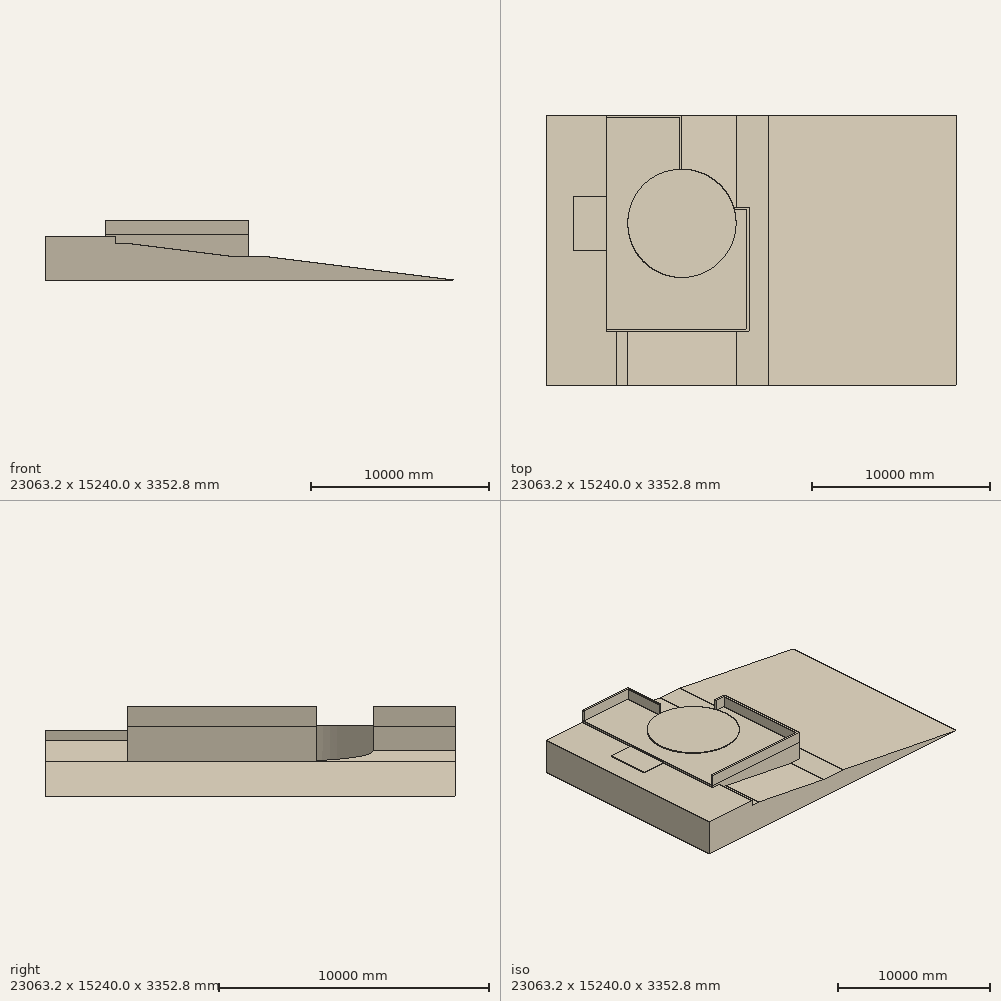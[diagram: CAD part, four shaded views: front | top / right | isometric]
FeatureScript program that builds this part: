
annotation { "Feature Type Name" : "Feature", "Feature Type Description" : "" }
export const myFeature = defineFeature(function(context is Context, id is Id, definition is map)
    precondition{}
    {
        {
            var Q0;
            Q0=qCreatedBy(makeId("Top.planeOp"),FACE);
            var sketch = newSketch(context, id + "F0", { "sketchPlane" : qUnion([Q0])});
            skCircle(sketch, "E0", {"center": v(0, 0) * mm, "radius": 3048 * mm});
            skSolve(sketch);
        }
        {
            var Q0;
            Q0=makeQuery(id+"F0.imprint","IMPRINT",FACE,{"disambiguationData":[TD([[makeQuery(id+"F0.imprint","IMPRINT",EDGE,{"derivedFrom":sQuery(id+"F0.wireOp",EDGE,"E0")}),1.0]])]});
            extrude(context, id + "F1", {"entities" : qUnion([Q0]), "depth" : 1320.8 * mm, "offsetDistance" : 25.4 * mm});
        }
        {
            var Q0;
            Q0=qCreatedBy(makeId("Front.planeOp"),FACE);
            var sketch = newSketch(context, id + "F2", { "sketchPlane" : qUnion([Q0])});
            skLineSegment(sketch, "E1", {"start": v(-3048, 0) * mm, "end": v(-3048, 1320.8) * mm});
            skLineSegment(sketch, "E2", {"start": v(3048, 1320.8) * mm, "end": v(3048, 0) * mm});
            skLineSegment(sketch, "E3", {"start": v(-3048, 762) * mm, "end": v(-3657.6, 762) * mm});
            skLineSegment(sketch, "E4", {"start": v(-3048, 762) * mm, "end": v(3048, 0) * mm});
            skLineSegment(sketch, "E5", {"start": v(-3657.6, 1117.6) * mm, "end": v(-5459.43, 1117.6) * mm});
            skLineSegment(sketch, "E6", {"start": v(-3657.6, 1117.6) * mm, "end": v(-3657.6, 762) * mm});
            skLineSegment(sketch, "E7", {"start": v(-5459.43, 1117.6) * mm, "end": v(-7620, 1117.6) * mm});
            skLineSegment(sketch, "E8", {"start": v(-7620, 1117.6) * mm, "end": v(-7620, -1320.8) * mm});
            skLineSegment(sketch, "E9", {"start": v(-7620, -1320.8) * mm, "end": v(15443.2, -1320.8) * mm});
            skLineSegment(sketch, "E10", {"start": v(3048, 0) * mm, "end": v(4876.8, 0) * mm});
            skLineSegment(sketch, "E11", {"start": v(4876.8, 0) * mm, "end": v(15443.2, -1320.8) * mm});
            skPoint(sketch, "E12.orphan", {"position": v(-7620, 762) * mm});
            skLineSegment(sketch, "E13.0", {"start": v(-3048, 0) * mm, "end": v(3048, 0) * mm, "construction": true});
            skSolve(sketch);
        }
        {
            var Q0;
            Q0 = qSketchRegion(id + "F2", true);
            extrude(context, id + "F3", {"entities" : qUnion([Q0]), "depth" : 9144 * mm, "offsetDistance" : 25.4 * mm});
        }
        {
            var Q0;
            Q0=makeQuery(id+"F3.opExtrude","CAP_FACE",FACE,{"disambiguationData":[OSD([sQuery(id+"F2.wireOp",EDGE,"E3"),sQuery(id+"F2.wireOp",EDGE,"E4"),sQuery(id+"F2.wireOp",EDGE,"E5"),sQuery(id+"F2.wireOp",EDGE,"E6"),sQuery(id+"F2.wireOp",EDGE,"E7"),sQuery(id+"F2.wireOp",EDGE,"E8"),sQuery(id+"F2.wireOp",EDGE,"E9"),sQuery(id+"F2.wireOp",EDGE,"E10"),sQuery(id+"F2.wireOp",EDGE,"E11")])],"isStart":true});
            extrude(context, id + "F4", {"entities" : qUnion([Q0]), "operationType" : NewBodyOperationType.ADD, "depth" : 6096 * mm, "offsetDistance" : 25.4 * mm});
        }
        {
            var Q0;
            Q0=makeQuery(id+"F1.opExtrude","CAP_FACE",FACE,{"disambiguationData":[OSD([sQuery(id+"F0.wireOp",EDGE,"E0")])],"isStart":false});
            cPlane(context, id + "F5", {"entities" : qUnion([Q0]), "cplaneType" : CPlaneType.OFFSET, "offset" : 50.8 * mm, "oppositeDirection" : true, "width" : 152.4 * mm, "height" : 152.4 * mm});
        }
        {
            var Q0;
            Q0=qCreatedBy(id+"F5.planeOp",FACE);
            var sketch = newSketch(context, id + "F6", { "sketchPlane" : qUnion([Q0])});
            skCircle(sketch, "E14.0", {"center": v(0, 0) * mm, "radius": 3048 * mm});
            skLineSegment(sketch, "E15.bottom", {"start": v(-4267.2, 6096) * mm, "end": v(0, 6096) * mm});
            skLineSegment(sketch, "E15.top", {"start": v(-4267.2, -6096) * mm, "end": v(3810, -6096) * mm});
            skLineSegment(sketch, "E15.left", {"start": v(-4267.2, 6096) * mm, "end": v(-4267.2, -6096) * mm});
            skLineSegment(sketch, "E15.right", {"start": v(3810, 914.4) * mm, "end": v(3810, -6096) * mm});
            skLineSegment(sketch, "E16", {"start": v(0, 3048) * mm, "end": v(0, 6096) * mm});
            skLineSegment(sketch, "E17", {"start": v(2907.6, 914.4) * mm, "end": v(3810, 914.4) * mm});
            skSolve(sketch);
        }
        {
            var Q0;
            Q0=makeQuery(id+"F6.imprint","IMPRINT",FACE,{"disambiguationData":[TD([[makeQuery(id+"F6.imprint","IMPRINT",EDGE,{"derivedFrom":sQuery(id+"F6.wireOp",EDGE,"E15.bottom")}),-1.0]])]});
            extrude(context, id + "F7", {"entities" : qUnion([Q0]), "endBound" : BoundingType.UP_TO_NEXT, "oppositeDirection" : true, "depth" : 25.4 * mm, "offsetDistance" : 25.4 * mm});
        }
        {
            var Q0;
            Q0=makeQuery(id+"F7.opExtrude","CAP_FACE",FACE,{"disambiguationData":[OSD([sQuery(id+"F6.wireOp",EDGE,"E14.0"),sQuery(id+"F6.wireOp",EDGE,"E15.bottom"),sQuery(id+"F6.wireOp",EDGE,"E15.top"),sQuery(id+"F6.wireOp",EDGE,"E15.left"),sQuery(id+"F6.wireOp",EDGE,"E15.right"),sQuery(id+"F6.wireOp",EDGE,"E16"),sQuery(id+"F6.wireOp",EDGE,"E17")])],"isStart":true});
            var sketch = newSketch(context, id + "F8", { "sketchPlane" : qUnion([Q0])});
            skLineSegment(sketch, "E18.0.0", {"start": v(3810, 914.4) * mm, "end": v(2907.6, 914.4) * mm});
            skArc(sketch, "E18.0.1", {"start": v(2907.6, 914.4) * mm, "mid": v(-1803.22, -2457.38) * mm, "end": v(0, 3048) * mm});
            skLineSegment(sketch, "E18.0.2", {"start": v(0, 3048) * mm, "end": v(0, 6096) * mm});
            skLineSegment(sketch, "E18.0.3", {"start": v(0, 6096) * mm, "end": v(-4267.2, 6096) * mm});
            skLineSegment(sketch, "E18.0.4", {"start": v(-4267.2, 6096) * mm, "end": v(-4267.2, -6096) * mm});
            skLineSegment(sketch, "E18.0.5", {"start": v(-4267.2, -6096) * mm, "end": v(3810, -6096) * mm});
            skLineSegment(sketch, "E18.0.6", {"start": v(3810, -6096) * mm, "end": v(3810, 914.4) * mm});
            skLineSegment(sketch, "E19.0", {"start": v(3657.6, -5943.6) * mm, "end": v(3657.6, 762) * mm});
            skLineSegment(sketch, "E19.1", {"start": v(-4267.2, -5943.6) * mm, "end": v(3657.6, -5943.6) * mm});
            skLineSegment(sketch, "E19.3", {"start": v(-152.4, 3044.19) * mm, "end": v(-152.4, 5943.6) * mm});
            skLineSegment(sketch, "E19.4", {"start": v(-152.4, 5943.6) * mm, "end": v(-4267.2, 5943.6) * mm});
            skLineSegment(sketch, "E19.5", {"start": v(3657.6, 762) * mm, "end": v(2951.21, 762) * mm});
            skSolve(sketch);
        }
        {
            var Q0;
            {var subQ4=sQuery(id+"F8.wireOp",EDGE,"E18.0.0");Q0=makeQuery(id+"F8.imprint","IMPRINT",FACE,{"disambiguationData":[TD([[makeQuery(id+"F8.imprint","IMPRINT",EDGE,{"derivedFrom":subQ4}),-1.0]])]});}
            var Q1;
            {var subQ3=sQuery(id+"F8.wireOp",EDGE,"E18.0.2");Q1=makeQuery(id+"F8.imprint","IMPRINT",FACE,{"disambiguationData":[TD([[makeQuery(id+"F8.imprint","IMPRINT",EDGE,{"derivedFrom":subQ3}),1.0]])]});}
            extrude(context, id + "F9", {"entities" : qUnion([Q0, Q1]), "depth" : 762 * mm, "offsetDistance" : 25.4 * mm});
        }
        {
            var Q0;
            {var subQ0=sQuery(id+"F2.wireOp",EDGE,"E7");var subQ1=sQuery(id+"F2.wireOp",EDGE,"E5");Q0=makeQuery(id+"F4.boolean.opBoolean","MERGE",FACE,{"derivedFrom":[makeQuery(id+"F3.opExtrude","SWEPT_FACE",FACE,{"disambiguationData":[OSD([subQ1,subQ0])]}),makeQuery(id+"F4.opExtrude","SWEPT_FACE",FACE,{"disambiguationData":[OSD([subQ1,subQ0])]})]});}
            var sketch = newSketch(context, id + "F10", { "sketchPlane" : qUnion([Q0])});
            skLineSegment(sketch, "E20.bottom", {"start": v(-4267.2, 1524) * mm, "end": v(-6096, 1524) * mm});
            skLineSegment(sketch, "E20.top", {"start": v(-4267.2, -1524) * mm, "end": v(-6096, -1524) * mm});
            skLineSegment(sketch, "E20.left", {"start": v(-4267.2, 1524) * mm, "end": v(-4267.2, -1524) * mm});
            skLineSegment(sketch, "E20.right", {"start": v(-6096, 1524) * mm, "end": v(-6096, -1524) * mm});
            skSolve(sketch);
        }
        {
            var Q0;
            Q0 = qSketchRegion(id + "F10", true);
            extrude(context, id + "F11", {"entities" : qUnion([Q0]), "depth" : 50.8 * mm, "offsetDistance" : 25.4 * mm});
        }
    });
